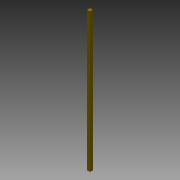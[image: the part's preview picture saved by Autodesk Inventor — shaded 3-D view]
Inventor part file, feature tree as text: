
AUTODESK INVENTOR PART (.ipt)
format: ipt  version: 2013 (Build 170138000, 138)  size: 64,512 bytes
history: native  units: mm
features: extrude x1, sketch x1
ambient origin geometry x8: Origin, YZ Plane, XZ Plane, XY Plane, X Axis, Y Axis, Z Axis, Center Point
bodies: Solid1 (feature_tree)
feature tree (2):
  extrude  "Extrusion1"  Depth=10.0mm
  sketch  "Sketch1"  dims[d0=10.0mm d1=10.0mm d2=470.0mm d3=0.0mm]
